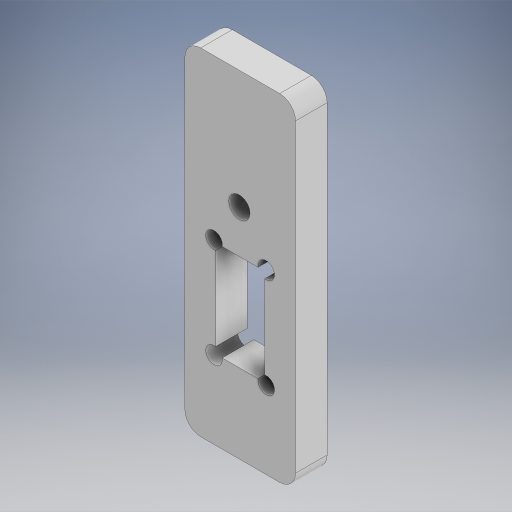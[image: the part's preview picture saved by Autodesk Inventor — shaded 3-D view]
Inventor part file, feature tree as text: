
AUTODESK INVENTOR PART (.ipt)
format: ipt  version: 2024 (Build 280153000, 153)  size: 330,240 bytes
history: native  units: mm
features: other x5, sketch x3, reference x3, extrude x2, projected_geometry x2, fillet x1, hole x1
ambient origin geometry x8: Origin, YZ Plane, XZ Plane, XY Plane, X Axis, Y Axis, Z Axis, Center Point
bodies: Body1 (feature_tree)
feature tree (17):
  other  "솔리드1"
  other  "작업 평면1"
  extrude  "돌출1"  Depth=0.3mm
  fillet  "모깎기1"  Radius=2.1mm
  extrude  "돌출2"  Depth=2.1mm
  hole  "구멍1"  [1 undecoded]
  sketch  "스케치1"
  reference  "참조1"
  reference  "참조2"
  reference  "참조3"
  sketch  "스케치2"
  projected_geometry  "투영된 루프1"
  sketch  "스케치3"
  projected_geometry  "투영된 루프2"
  other  "<userpath>\Desktop\ZIG\조립품1.iam"
  other  "조립품1.iam"
  other  "battery_up:1"
note: 1 required parameter value undecoded (feature->parameter linkage not recoverable at this tier; creation-order binding heuristic only, values carry confidence <= 0.55)
